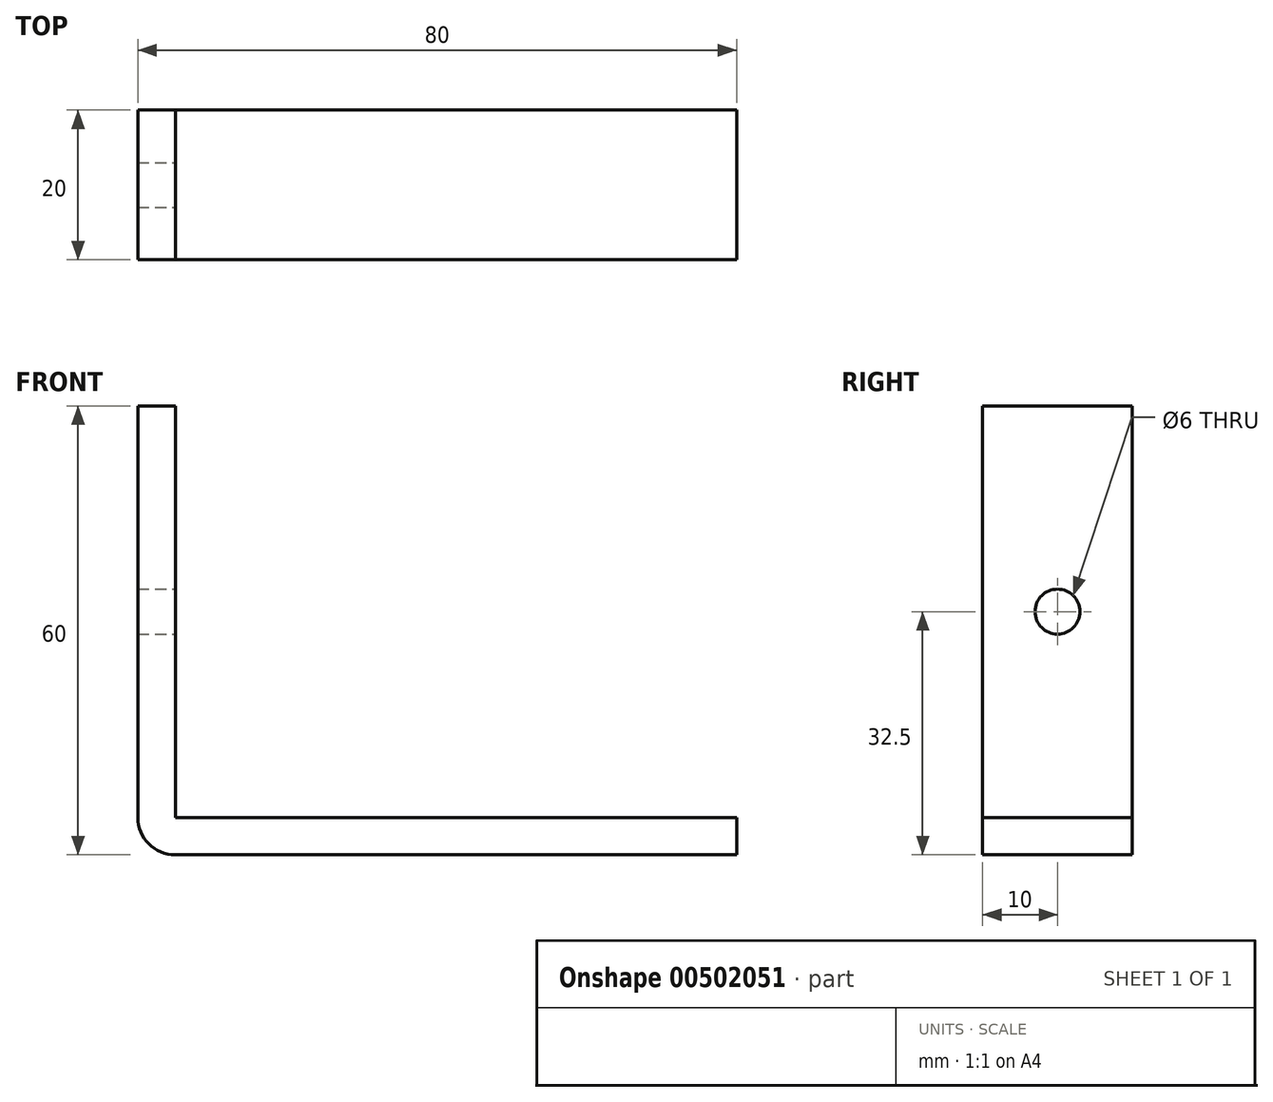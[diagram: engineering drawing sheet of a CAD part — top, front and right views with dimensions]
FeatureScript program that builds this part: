
annotation { "Feature Type Name" : "Feature", "Feature Type Description" : "" }
export const myFeature = defineFeature(function(context is Context, id is Id, definition is map)
    precondition{}
    {
        {
            var Q0;
            Q0=qCreatedBy(makeId("Top.planeOp"),FACE);
            var sketch = newSketch(context, id + "F0", { "sketchPlane" : qUnion([Q0])});
            skLineSegment(sketch, "E0.bottom", {"start": v(0, 0) * mm, "end": v(5, 0) * mm});
            skLineSegment(sketch, "E0.top", {"start": v(0, -20) * mm, "end": v(5, -20) * mm});
            skLineSegment(sketch, "E0.left", {"start": v(0, 0) * mm, "end": v(0, -20) * mm});
            skLineSegment(sketch, "E0.right", {"start": v(5, 0) * mm, "end": v(5, -20) * mm});
            skSolve(sketch);
        }
        {
            var Q0;
            Q0=qCreatedBy(makeId("Front.planeOp"),FACE);
            var sketch = newSketch(context, id + "F1", { "sketchPlane" : qUnion([Q0])});
            skLineSegment(sketch, "E1", {"start": v(0, 0) * mm, "end": v(0, -55) * mm});
            skLineSegment(sketch, "E2", {"start": v(5, -60) * mm, "end": v(80, -60) * mm});
            skPoint(sketch, "E3.visualSharp", {"position": v(0, -60) * mm});
            skArc(sketch, "E3.filletArc", {"start": v(0, -55) * mm, "mid": v(1.46, -58.54) * mm, "end": v(5, -60) * mm});
            skSolve(sketch);
        }
        {
            var Q0;
            Q0=makeQuery(id+"F0.imprint","IMPRINT",FACE,{"disambiguationData":[TD([[makeQuery(id+"F0.imprint","IMPRINT",EDGE,{"derivedFrom":sQuery(id+"F0.wireOp",EDGE,"E0.bottom")}),-1.0]])]});
            var Q1;
            Q1=sQuery(id+"F1.wireOp",EDGE,"E1");
            var Q2;
            Q2=sQuery(id+"F1.wireOp",EDGE,"E3.filletArc");
            var Q3;
            Q3=sQuery(id+"F1.wireOp",EDGE,"E2");
            sweep(context, id + "F2", {"profiles" : qUnion([Q0]), "path" : qUnion([Q1, Q2, Q3])});
        }
        {
            var Q0;
            Q0=makeQuery(id+"F2.opSweep","SWEPT_FACE",FACE,{"disambiguationData":[OSD([sQuery(id+"F0.wireOp",EDGE,"E0.right"),sQuery(id+"F1.wireOp",EDGE,"E1")])]});
            var sketch = newSketch(context, id + "F3", { "sketchPlane" : qUnion([Q0])});
            skPoint(sketch, "E4", {"position": v(-10, -27.5) * mm});
            skPoint(sketch, "E4.positionSnap0", {"position": v(0, -27.5) * mm});
            skPoint(sketch, "E4.positionSnap1", {"position": v(-10, 0) * mm});
            skSolve(sketch);
        }
        {
            var Q0;
            Q0=sQuery(id+"F3.wireOp",VERTEX,"E4");
            var Q1;
            Q1=makeQuery(id+"F2.opSweep","SWEPT_BODY",BODY,{"disambiguationData":[OSD([sQuery(id+"F0.wireOp",EDGE,"E0.bottom"),sQuery(id+"F0.wireOp",EDGE,"E0.top"),sQuery(id+"F0.wireOp",EDGE,"E0.left"),sQuery(id+"F0.wireOp",EDGE,"E0.right"),sQuery(id+"F1.wireOp",EDGE,"E2")])]});
            hole(context, id + "F4", {"style" : HoleStyle.SIMPLE, "endStyle" : HoleEndStyle.THROUGH, "holeDiameter" : 6 * mm, "isTappedThrough" : true, "tappedDepth" : 12 * mm, "tapClearance" : 3, "locations" : qUnion([Q0]), "scope" : qUnion([Q1])});
        }
    });
